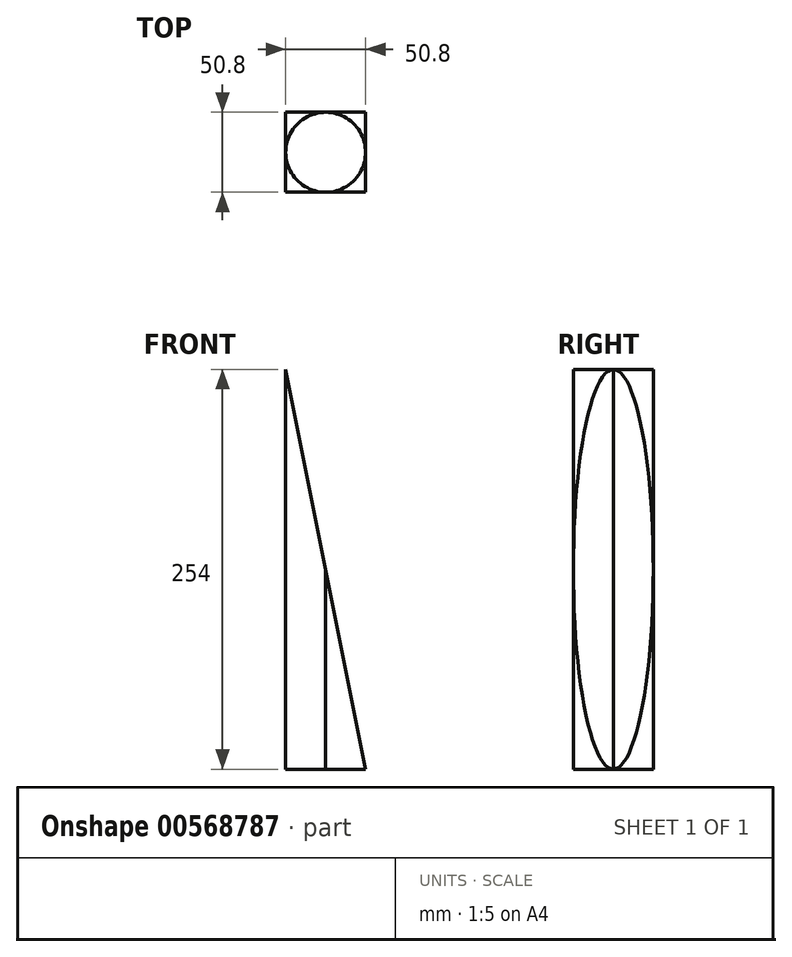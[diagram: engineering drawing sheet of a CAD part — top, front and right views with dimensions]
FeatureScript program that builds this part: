
annotation { "Feature Type Name" : "Feature", "Feature Type Description" : "" }
export const myFeature = defineFeature(function(context is Context, id is Id, definition is map)
    precondition{}
    {
        {
            var Q0;
            Q0=qCreatedBy(makeId("Front.planeOp"),FACE);
            var sketch = newSketch(context, id + "F0", { "sketchPlane" : qUnion([Q0])});
            skLineSegment(sketch, "E0", {"start": v(-25.4, 0) * mm, "end": v(25.4, 0) * mm});
            skLineSegment(sketch, "E1", {"start": v(-25.4, 0) * mm, "end": v(-25.4, 254) * mm});
            skLineSegment(sketch, "E2", {"start": v(-25.4, 254) * mm, "end": v(25.4, 0) * mm});
            skSolve(sketch);
        }
        {
            var Q0;
            Q0 = qSketchRegion(id + "F0", true);
            extrude(context, id + "F1", {"entities" : qUnion([Q0]), "endBound" : BoundingType.SYMMETRIC, "depth" : 50.8 * mm, "offsetDistance" : 25.4 * mm});
        }
        {
            var Q0;
            Q0=makeQuery(id+"F1.opExtrude","SWEPT_FACE",FACE,{"disambiguationData":[OSD([sQuery(id+"F0.wireOp",EDGE,"E0")])]});
            var sketch = newSketch(context, id + "F2", { "sketchPlane" : qUnion([Q0])});
            skCircle(sketch, "E3", {"center": v(0, 0) * mm, "radius": 25.4 * mm});
            skLineSegment(sketch, "E4.bottom", {"start": v(-25.4, 25.4) * mm, "end": v(-25.4, 25.4) * mm});
            skLineSegment(sketch, "E4.top", {"start": v(-25.4, -25.4) * mm, "end": v(-25.4, -25.4) * mm});
            skLineSegment(sketch, "E4.left", {"start": v(-25.4, 25.4) * mm, "end": v(-25.4, -25.4) * mm});
            skLineSegment(sketch, "E4.right", {"start": v(-25.4, 25.4) * mm, "end": v(-25.4, -25.4) * mm});
            skSolve(sketch);
        }
        {
            var Q0;
            {var subQ0=sQuery(id+"F2.wireOp",EDGE,"E3");var subQ1=sQuery(id+"F0.wireOp",EDGE,"E0");var subQ4=makeQuery(id+"F1.opExtrude","CAP_EDGE",EDGE,{"disambiguationData":[OSD([subQ1])],"isStart":false});var subQ5=makeQuery(id+"F2.imprint","INTERSECT",VERTEX,{"derivedFrom":[subQ4,subQ0]});Q0=makeQuery(id+"F2.imprint","IMPRINT",FACE,{"disambiguationData":[TD([[makeQuery(id+"F2.imprint","IMPRINT",EDGE,{"disambiguationData":[TD([[subQ5,-1.0]])],"derivedFrom":subQ0}),1.0]])]});}
            var Q1;
            {var subQ0=sQuery(id+"F2.wireOp",EDGE,"E3");var subQ1=sQuery(id+"F0.wireOp",EDGE,"E0");var subQ2=makeQuery(id+"F1.opExtrude","CAP_EDGE",EDGE,{"disambiguationData":[OSD([subQ1])],"isStart":true});var subQ3=makeQuery(id+"F2.imprint","INTERSECT",VERTEX,{"derivedFrom":[subQ2,subQ0]});Q1=makeQuery(id+"F2.imprint","IMPRINT",FACE,{"disambiguationData":[TD([[makeQuery(id+"F2.imprint","IMPRINT",EDGE,{"disambiguationData":[TD([[subQ3,1.0]])],"derivedFrom":subQ0}),1.0]])]});}
            var Q2;
            {var subQ0=sQuery(id+"F2.wireOp",EDGE,"E4.right");var subQ1=sQuery(id+"F2.wireOp",EDGE,"E3");var subQ2=makeQuery(id+"F2.imprint","INTERSECT",VERTEX,{"derivedFrom":[subQ1,subQ0]});Q2=makeQuery(id+"F2.imprint","IMPRINT",FACE,{"disambiguationData":[TD([[makeQuery(id+"F2.imprint","IMPRINT",EDGE,{"disambiguationData":[TD([[subQ2,1.0]])],"derivedFrom":subQ1}),1.0]])]});}
            var Q3;
            {var subQ0=sQuery(id+"F2.wireOp",EDGE,"E4.right");var subQ1=sQuery(id+"F2.wireOp",EDGE,"E3");var subQ2=makeQuery(id+"F2.imprint","INTERSECT",VERTEX,{"derivedFrom":[subQ1,subQ0]});Q3=makeQuery(id+"F2.imprint","IMPRINT",FACE,{"disambiguationData":[TD([[makeQuery(id+"F2.imprint","IMPRINT",EDGE,{"disambiguationData":[TD([[subQ2,-1.0]])],"derivedFrom":subQ1}),1.0]])]});}
            extrude(context, id + "F3", {"entities" : qUnion([Q0, Q1, Q2, Q3]), "operationType" : NewBodyOperationType.REMOVE, "oppositeDirection" : true, "depth" : 254 * mm, "offsetDistance" : 25.4 * mm});
        }
    });
